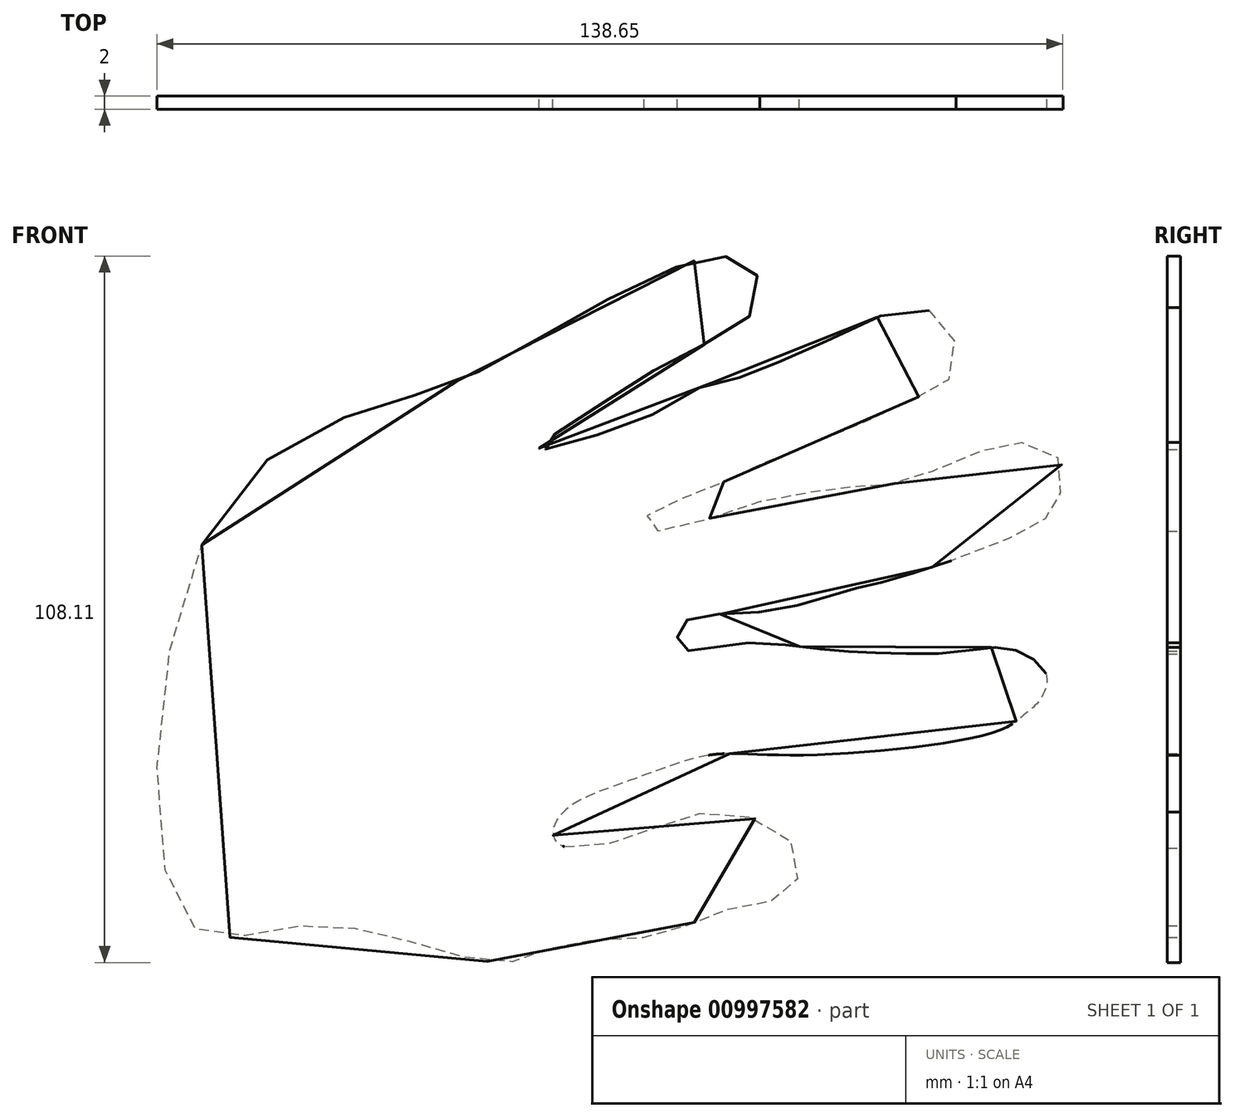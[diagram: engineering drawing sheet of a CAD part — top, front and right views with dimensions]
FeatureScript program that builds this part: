
annotation { "Feature Type Name" : "Feature", "Feature Type Description" : "" }
export const myFeature = defineFeature(function(context is Context, id is Id, definition is map)
    precondition{}
    {
        {
            var Q0;
            Q0=qCreatedBy(makeId("Front.planeOp"),FACE);
            var sketch = newSketch(context, id + "F0", { "sketchPlane" : qUnion([Q0])});
            skFitSpline(sketch, "E0", {"points": [v(-69.99, 3.5) * mm, v(-46.38, 23.66) * mm, v(-29.71, 29.1) * mm, v(-14.03, 37.68) * mm, v(4.12, 46.6) * mm, v(11.55, 47.42) * mm, v(15.18, 44.29) * mm, v(13.53, 38.18) * mm, v(3.96, 32.9) * mm, v(-5.12, 27.45) * mm, v(-15.85, 20.52) * mm, v(-18.32, 18.2) * mm, v(-12.88, 19.36) * mm, v(-1.32, 23.33) * mm, v(7.42, 28.11) * mm, v(12.87, 29.27) * mm, v(18.81, 31.74) * mm, v(28.38, 36.03) * mm, v(38.95, 39.83) * mm, v(44.4, 36.7) * mm, v(44.72, 29.43) * mm, v(39.6, 26.13) * mm, v(30.03, 21.67) * mm, v(15.34, 15.73) * mm, v(8.25, 12.43) * mm, v(0, 9.13) * mm, v(-2.31, 7.15) * mm, v(0, 5.67) * mm, v(11.88, 9.13) * mm, v(23.1, 11.6) * mm, v(31.68, 12.6) * mm, v(36.8, 13.1) * mm, v(47.53, 17.22) * mm, v(55.28, 19.2) * mm, v(61.23, 16.56) * mm, v(61.23, 10.95) * mm, v(59.25, 7.65) * mm, v(51.98, 3.85) * mm, v(36.3, -1.6) * mm, v(28.55, -3.58) * mm, v(15.67, -6.71) * mm, v(3.3, -8.7) * mm, v(3.63, -12.32) * mm, v(11.05, -11.66) * mm, v(25.08, -12.49) * mm, v(33.33, -12.98) * mm, v(44.4, -12.98) * mm, v(52.31, -12.16) * mm, v(56.44, -13.48) * mm, v(59.25, -16.28) * mm, v(58.25, -20.25) * mm, v(55.94, -22.4) * mm, v(51.65, -25.03) * mm, v(20.63, -28.66) * mm, v(7.59, -28.66) * mm, v(-3.8, -32.3) * mm, v(-15.19, -37.9) * mm, v(-15.52, -42.2) * mm, v(-3.3, -40.87) * mm, v(7.75, -37.4) * mm, v(20.3, -42.03) * mm, v(19.97, -49.62) * mm, v(10.56, -52.26) * mm, v(0, -56.22) * mm, v(-14.36, -57.54) * mm, v(-23.1, -60.35) * mm, v(-39.28, -56.88) * mm, v(-56.78, -55.07) * mm, v(-72.13, -54.24) * mm, v(-69.99, 3.5) * mm]});
            skSolve(sketch);
        }
        {
            var Q0;
            Q0=makeQuery(id+"F0.imprint","IMPRINT",FACE,{"disambiguationData":[TD([[makeQuery(id+"F0.imprint","IMPRINT",EDGE,{"derivedFrom":sQuery(id+"F0.wireOp",EDGE,"E0")}),-1.0]])]});
            extrude(context, id + "F1", {"entities" : qUnion([Q0]), "depth" : 2 * mm, "offsetDistance" : 25 * mm});
        }
    });
